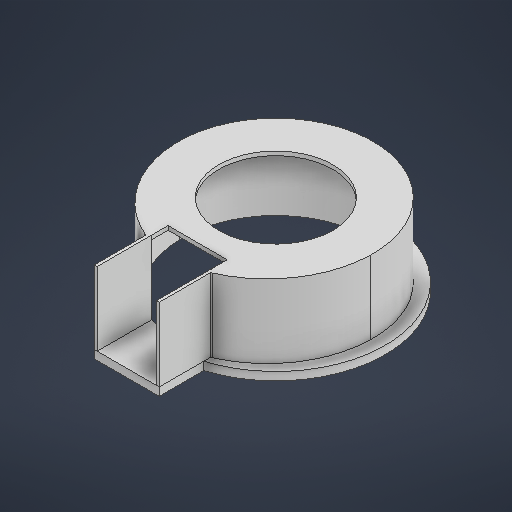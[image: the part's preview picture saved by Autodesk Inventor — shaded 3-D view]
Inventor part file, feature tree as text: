
AUTODESK INVENTOR PART (.ipt)
format: ipt  version: 2025 (Build 290162000, 162)  size: 269,312 bytes
history: native  units: in
note: dims shown in document units (in); Inventor stores cm internally (conversion verified against a paired STEP export)
features: extrude x3, sketch x3
ambient origin geometry x8: Origin, YZ Plane, XZ Plane, XY Plane, X Axis, Y Axis, Z Axis, Center Point
bodies: Solid1 (feature_tree)
feature tree (6):
  extrude  "Extrusion1"  Depth=0.3937in TaperAngle=0.0deg
  extrude  "Extrusion3"  Depth=3.1496in
  extrude  "Extrusion4"  Depth=0.1969in
  sketch  "Sketch1"  dims[d0=10.6299in d2=0.3937in d3=0.0in]
  sketch  "Sketch5"  dims[d4=0.1919in d7=3.1496in]
  sketch  "Sketch6"  dims[d9=9.0551in d13=2.1654in d16=0.1378in d17=0.1969in d20=0.1378in d24=0.1969in d26=2.1654in d27=0.1378in d28=3.563in d29=0.0in d30=5.5413in d31=0.1969in d32=0.0in d33=0.7874in d5=0.0197in d6=0.0344in d8=0.0344in d10=0.0344in d25=0.0197in]
